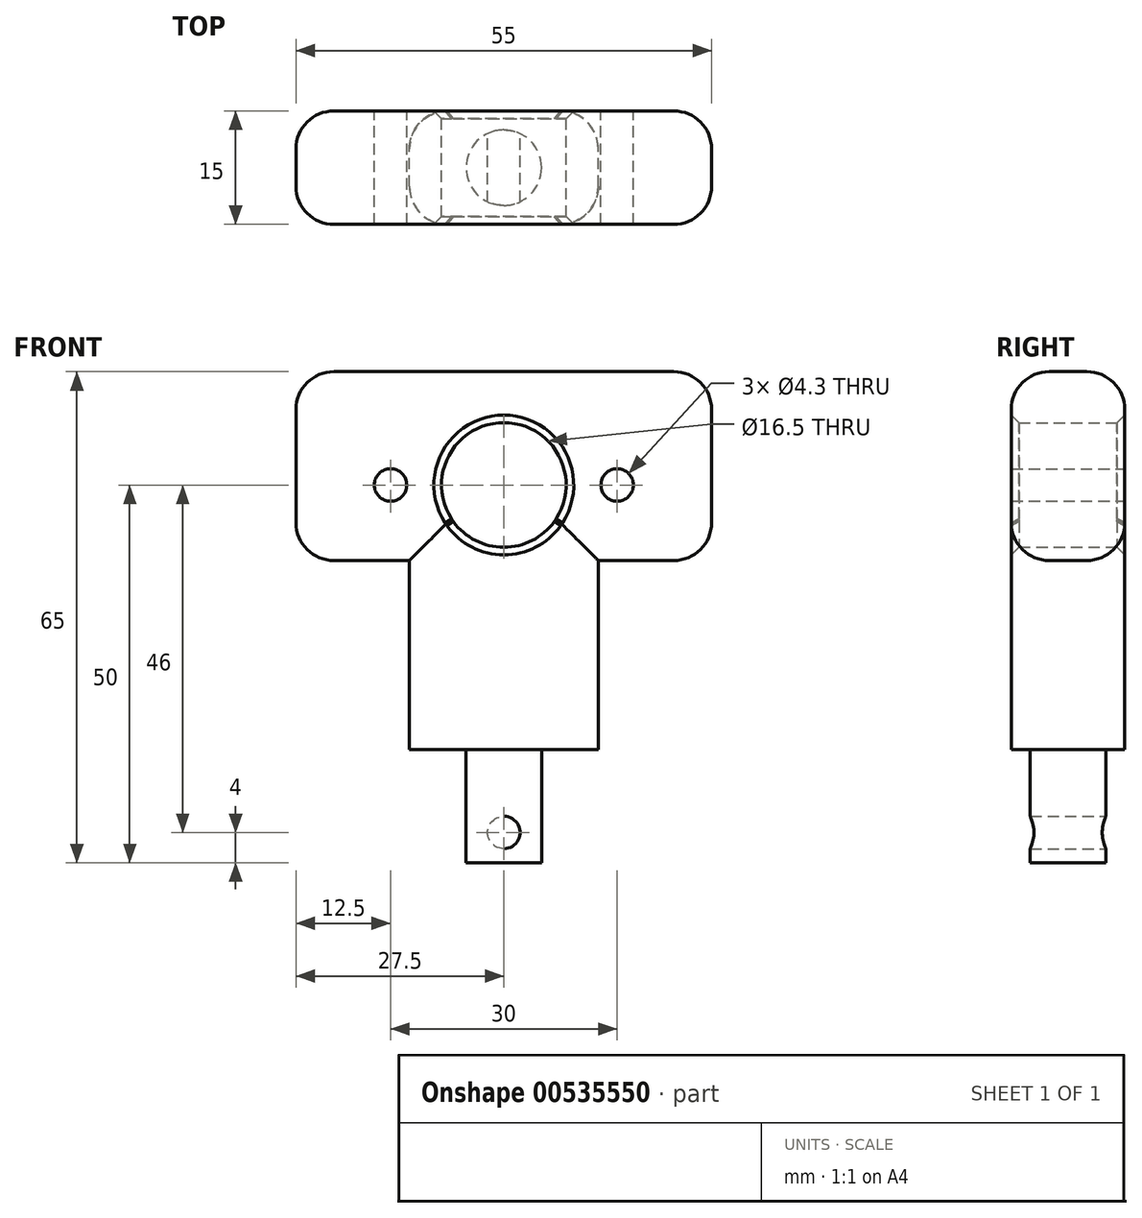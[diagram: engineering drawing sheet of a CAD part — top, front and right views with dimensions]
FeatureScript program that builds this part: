
annotation { "Feature Type Name" : "Feature", "Feature Type Description" : "" }
export const myFeature = defineFeature(function(context is Context, id is Id, definition is map)
    precondition{}
    {
        {
            var Q0;
            Q0=qCreatedBy(makeId("Front.planeOp"),FACE);
            var sketch = newSketch(context, id + "F0", { "sketchPlane" : qUnion([Q0])});
            skCircle(sketch, "E0", {"center": v(0, 0) * mm, "radius": 8.25 * mm});
            skLineSegment(sketch, "E1.bottom", {"start": v(-12.5, 15) * mm, "end": v(12.5, 15) * mm});
            skLineSegment(sketch, "E1.top", {"start": v(-12.5, -35) * mm, "end": v(12.5, -35) * mm});
            skLineSegment(sketch, "E1.left", {"start": v(-12.5, 15) * mm, "end": v(-12.5, -35) * mm});
            skLineSegment(sketch, "E1.right", {"start": v(12.5, 15) * mm, "end": v(12.5, -35) * mm});
            skLineSegment(sketch, "E2.bottom", {"start": v(-12.5, 15) * mm, "end": v(-27.5, 15) * mm});
            skLineSegment(sketch, "E2.top", {"start": v(-12.5, -10) * mm, "end": v(-27.5, -10) * mm});
            skLineSegment(sketch, "E2.left", {"start": v(-12.5, 15) * mm, "end": v(-12.5, -10) * mm});
            skLineSegment(sketch, "E2.right", {"start": v(-27.5, 15) * mm, "end": v(-27.5, -10) * mm});
            skLineSegment(sketch, "E3.MirrorCS", {"start": v(12.5, 15) * mm, "end": v(27.5, 15) * mm});
            skLineSegment(sketch, "E4.MirrorCS", {"start": v(27.5, 15) * mm, "end": v(27.5, -10) * mm});
            skLineSegment(sketch, "E5.MirrorCS", {"start": v(12.5, -10) * mm, "end": v(27.5, -10) * mm});
            skLineSegment(sketch, "E6.MirrorCS", {"start": v(12.5, 15) * mm, "end": v(12.5, -10) * mm});
            skSolve(sketch);
        }
        {
            var Q0;
            Q0 = qSketchRegion(id + "F0", true);
            extrude(context, id + "F1", {"entities" : qUnion([Q0]), "depth" : 15 * mm, "offsetDistance" : 25 * mm, "symmetric" : true});
        }
        {
            var Q0;
            Q0=qCreatedBy(makeId("Front.planeOp"),FACE);
            var sketch = newSketch(context, id + "F2", { "sketchPlane" : qUnion([Q0])});
            skCircle(sketch, "E7", {"center": v(-15, 0) * mm, "radius": 2.15 * mm});
            skCircle(sketch, "E8.MirrorC", {"center": v(15, 0) * mm, "radius": 2.15 * mm});
            skSolve(sketch);
        }
        {
            var Q0;
            Q0 = qSketchRegion(id + "F2", true);
            extrude(context, id + "F3", {"entities" : qUnion([Q0]), "operationType" : NewBodyOperationType.REMOVE, "depth" : 34.5 * mm, "offsetDistance" : 25 * mm, "symmetric" : true});
        }
        {
            var Q0;
            Q0=qCreatedBy(makeId("Front.planeOp"),FACE);
            var sketch = newSketch(context, id + "F4", { "sketchPlane" : qUnion([Q0])});
            skLineSegment(sketch, "E9.bottom", {"start": v(-5, -35) * mm, "end": v(5, -35) * mm});
            skLineSegment(sketch, "E9.top", {"start": v(-5, -50) * mm, "end": v(5, -50) * mm});
            skLineSegment(sketch, "E9.left", {"start": v(-5, -35) * mm, "end": v(-5, -50) * mm});
            skLineSegment(sketch, "E9.right", {"start": v(5, -35) * mm, "end": v(5, -50) * mm});
            skPoint(sketch, "E9.middle", {"position": v(0, -42.5) * mm});
            skCircle(sketch, "E10", {"center": v(0, -46) * mm, "radius": 2.15 * mm});
            skSolve(sketch);
        }
        {
            var Q0;
            Q0 = qSketchRegion(id + "F4", true);
            extrude(context, id + "F5", {"entities" : qUnion([Q0]), "operationType" : NewBodyOperationType.ADD, "depth" : 10 * mm, "offsetDistance" : 25 * mm, "symmetric" : true});
        }
        {
            var Q0;
            Q0=makeQuery(id+"F5.opExtrude","CAP_EDGE",EDGE,{"disambiguationData":[OSD([sQuery(id+"F4.wireOp",EDGE,"E9.left")])],"isStart":false});
            var Q1;
            Q1=makeQuery(id+"F5.opExtrude","CAP_EDGE",EDGE,{"disambiguationData":[OSD([sQuery(id+"F4.wireOp",EDGE,"E9.right")])],"isStart":false});
            var Q2;
            Q2=makeQuery(id+"F5.opExtrude","CAP_EDGE",EDGE,{"disambiguationData":[OSD([sQuery(id+"F4.wireOp",EDGE,"E9.right")])],"isStart":true});
            var Q3;
            Q3=makeQuery(id+"F5.opExtrude","CAP_EDGE",EDGE,{"disambiguationData":[OSD([sQuery(id+"F4.wireOp",EDGE,"E9.left")])],"isStart":true});
            var Q4;
            Q4=makeQuery(id+"F1.opExtrude","SWEPT_EDGE",EDGE,{"disambiguationData":[OSD([sQuery(id+"F0.wireOp",EDGE,"E2.bottom"),sQuery(id+"F0.wireOp",EDGE,"E2.right")])]});
            var Q5;
            Q5=makeQuery(id+"F1.opExtrude","SWEPT_EDGE",EDGE,{"disambiguationData":[OSD([sQuery(id+"F0.wireOp",EDGE,"E3.MirrorCS"),sQuery(id+"F0.wireOp",EDGE,"E4.MirrorCS")])]});
            var Q6;
            Q6=makeQuery(id+"F1.opExtrude","SWEPT_EDGE",EDGE,{"disambiguationData":[OSD([sQuery(id+"F0.wireOp",EDGE,"E4.MirrorCS"),sQuery(id+"F0.wireOp",EDGE,"E5.MirrorCS")])]});
            var Q7;
            Q7=makeQuery(id+"F1.opExtrude","SWEPT_EDGE",EDGE,{"disambiguationData":[OSD([sQuery(id+"F0.wireOp",EDGE,"E2.top"),sQuery(id+"F0.wireOp",EDGE,"E2.right")])]});
            var Q8;
            Q8=makeQuery(id+"F1.opExtrude","CAP_EDGE",EDGE,{"disambiguationData":[OSD([sQuery(id+"F0.wireOp",EDGE,"E2.right")])],"isStart":false});
            var Q9;
            Q9=makeQuery(id+"F1.opExtrude","CAP_EDGE",EDGE,{"disambiguationData":[OSD([sQuery(id+"F0.wireOp",EDGE,"E1.bottom"),sQuery(id+"F0.wireOp",EDGE,"E2.bottom"),sQuery(id+"F0.wireOp",EDGE,"E3.MirrorCS")])],"isStart":false});
            var Q10;
            Q10=makeQuery(id+"F1.opExtrude","CAP_EDGE",EDGE,{"disambiguationData":[OSD([sQuery(id+"F0.wireOp",EDGE,"E4.MirrorCS")])],"isStart":false});
            var Q11;
            Q11=makeQuery(id+"F1.opExtrude","CAP_EDGE",EDGE,{"disambiguationData":[OSD([sQuery(id+"F0.wireOp",EDGE,"E1.right")])],"isStart":false});
            var Q12;
            Q12=makeQuery(id+"F1.opExtrude","CAP_EDGE",EDGE,{"disambiguationData":[OSD([sQuery(id+"F0.wireOp",EDGE,"E5.MirrorCS")])],"isStart":false});
            var Q13;
            Q13=makeQuery(id+"F1.opExtrude","CAP_EDGE",EDGE,{"disambiguationData":[OSD([sQuery(id+"F0.wireOp",EDGE,"E2.top")])],"isStart":false});
            var Q14;
            Q14=makeQuery(id+"F1.opExtrude","CAP_EDGE",EDGE,{"disambiguationData":[OSD([sQuery(id+"F0.wireOp",EDGE,"E1.left")])],"isStart":false});
            var Q15;
            Q15=makeQuery(id+"F1.opExtrude","CAP_EDGE",EDGE,{"disambiguationData":[OSD([sQuery(id+"F0.wireOp",EDGE,"E1.bottom"),sQuery(id+"F0.wireOp",EDGE,"E2.bottom"),sQuery(id+"F0.wireOp",EDGE,"E3.MirrorCS")])],"isStart":true});
            var Q16;
            Q16=makeQuery(id+"F1.opExtrude","CAP_EDGE",EDGE,{"disambiguationData":[OSD([sQuery(id+"F0.wireOp",EDGE,"E2.right")])],"isStart":true});
            var Q17;
            Q17=makeQuery(id+"F1.opExtrude","CAP_EDGE",EDGE,{"disambiguationData":[OSD([sQuery(id+"F0.wireOp",EDGE,"E2.top")])],"isStart":true});
            var Q18;
            Q18=makeQuery(id+"F1.opExtrude","CAP_EDGE",EDGE,{"disambiguationData":[OSD([sQuery(id+"F0.wireOp",EDGE,"E1.left")])],"isStart":true});
            var Q19;
            Q19=makeQuery(id+"F1.opExtrude","CAP_EDGE",EDGE,{"disambiguationData":[OSD([sQuery(id+"F0.wireOp",EDGE,"E1.right")])],"isStart":true});
            var Q20;
            Q20=makeQuery(id+"F1.opExtrude","CAP_EDGE",EDGE,{"disambiguationData":[OSD([sQuery(id+"F0.wireOp",EDGE,"E4.MirrorCS")])],"isStart":true});
            var Q21;
            Q21=makeQuery(id+"F1.opExtrude","CAP_EDGE",EDGE,{"disambiguationData":[OSD([sQuery(id+"F0.wireOp",EDGE,"E5.MirrorCS")])],"isStart":true});
            fillet(context, id + "F6", {"entities" : qUnion([Q0, Q1, Q2, Q3, Q4, Q5, Q6, Q7, Q8, Q9, Q10, Q11, Q12, Q13, Q14, Q15, Q16, Q17, Q18, Q19, Q20, Q21]), "radius" : 5 * mm, "tangentPropagation" : true, "allowEdgeOverflow" : false});
        }
        {
            var Q0;
            Q0=makeQuery(id+"F1.opExtrude","CAP_EDGE",EDGE,{"disambiguationData":[OSD([sQuery(id+"F0.wireOp",EDGE,"E0")])],"isStart":true});
            var Q1;
            Q1=makeQuery(id+"F1.opExtrude","CAP_EDGE",EDGE,{"disambiguationData":[OSD([sQuery(id+"F0.wireOp",EDGE,"E0")])],"isStart":false});
            chamfer(context, id + "F7", {"entities" : qUnion([Q0, Q1]), "width" : 1 * mm, "tangentPropagation" : true});
        }
    });
